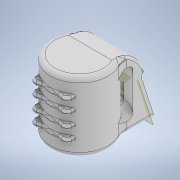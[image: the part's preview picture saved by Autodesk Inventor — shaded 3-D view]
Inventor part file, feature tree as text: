
AUTODESK INVENTOR PART (.ipt)
format: ipt  version: 2021.1 (Build 251245010, 245A)  size: 642,560 bytes
history: native  units: mm
features: extrude x8, sketch x7, fillet x5, revolve x1, plane x1
ambient origin geometry x8: Origin, YZ Plane, XZ Plane, XY Plane, X Axis, Y Axis, Z Axis, Center Point
bodies: Volumenkörper1 (feature_tree)
feature tree (22):
  extrude  "Extrusion1"  Depth=30.0mm TaperAngle=0.0deg
  extrude  "Extrusion2"  Depth=2.0mm
  extrude  "Extrusion3"  Depth=30.0mm
  fillet  "Rundung1"  Radius=13.25mm
  fillet  "Rundung2"  Radius=14.5mm
  extrude  "Extrusion4"  Depth=40.0mm
  revolve  "Umdrehung1"
  fillet  "Rundung3"  Radius=10.05mm
  extrude  "Extrusion5"  Depth=2.0mm
  extrude  "Extrusion6"  Depth=0.9mm
  plane  "Arbeitsebene1"
  extrude  "Extrusion7"  Depth=22.5mm
  extrude  "Extrusion8"  Depth=20.0mm
  fillet  "Rundung5"  Radius=10.0mm
  fillet  "Rundung6"  Radius=25.0mm
  sketch  "Skizze1"  dims[d0=25.0mm d1=30.0mm d2=0.0mm]
  sketch  "Skizze2"  dims[d3=16.0mm d4=2.0mm]
  sketch  "Skizze3"  dims[d5=8.0mm d6=30.0mm d8=13.25mm]
  sketch  "Skizze4"  dims[d9=20.0mm d11=5.5mm d12=10.0mm d14=10.0mm]
  sketch  "Skizze6"  dims[d16=20.0mm d18=5.0mm d19=10.0mm d21=10.0mm]
  sketch  "Skizze9"  dims[d23=20.0mm d25=5.0mm d26=10.0mm d28=10.0mm d30=14.5mm d31=0.0mm]
  sketch  "Skizze10"  dims[d32=32.5mm d33=40.0mm d34=10.05mm d35=0.0mm d36=2.0mm d37=0.9mm d38=22.5mm d39=20.0mm d40=10.0mm d41=25.0mm d42=0.0mm d44=16.0mm d45=4.0mm d46=180.0deg d47=2.0mm d48=3.141593mm d49=20.0mm d50=1.5mm d51=80.0mm d52=48.0mm d53=0.0mm d54=0.0mm d55=3.7mm d56=10.0mm d57=12.0mm d58=13.0mm d59=0.0mm d60=-2.0mm d61=6.0mm d62=3.8mm d63=0.0mm d65=12.5mm d66=2.0mm d67=14.0mm d68=0.0mm d69=0.0mm d70=1.0mm d71=10.0mm d72=6.243543mm d73=0.0mm d74=0.872665mm]
